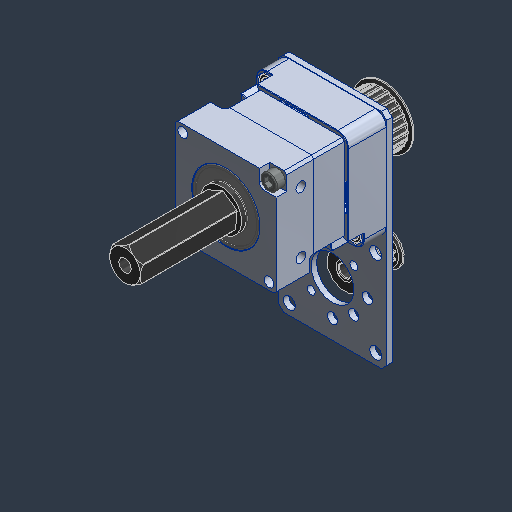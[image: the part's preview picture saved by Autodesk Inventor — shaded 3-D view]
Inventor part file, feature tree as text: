
AUTODESK INVENTOR PART (.ipt)
format: ipt  version: 2024.3 (Build 283343000, 343)  size: 5,744,640 bytes
history: native  units: mm (DEFAULTED — no unit token found)
features: other x17, direct_edit x1, revolve x1
ambient origin geometry x8: Origin, YZ Plane, XZ Plane, XY Plane, X Axis, Y Axis, Z Axis, Center Point
bodies: Solid2 (feature_tree), Solid3 (feature_tree), Solid4 (feature_tree), Solid5 (feature_tree), Solid6 (feature_tree), Solid7 (feature_tree), Solid8 (feature_tree), Solid9 (feature_tree), Solid10 (feature_tree), Solid11 (feature_tree), Solid12 (feature_tree), Solid13 (feature_tree), Solid14 (feature_tree), Solid15 (feature_tree), Solid16 (feature_tree), Solid17 (feature_tree), Solid18 (feature_tree)
feature tree (19):
  direct_edit  "Direct Edit1"
  other  "NAUO2:1"
  other  "NAUO3:1"
  other  "NAUO4:1"
  other  "NAUO5:1"
  other  "NAUO6:1"
  other  "NAUO7:1"
  other  "NAUO8:1"
  other  "NAUO9:1"
  other  "NAUO10:1"
  other  "NAUO11:1"
  other  "NAUO12:1"
  other  "NAUO13:1"
  other  "NAUO14:1"
  other  "NAUO16:1"
  other  "NAUO17:1"
  other  "NAUO19:1"
  other  "NAUO20:1"
  revolve  "Rotate1"  [1 undecoded]
note: 1 required parameter value undecoded (feature->parameter linkage not recoverable at this tier; creation-order binding heuristic only, values carry confidence <= 0.55)
